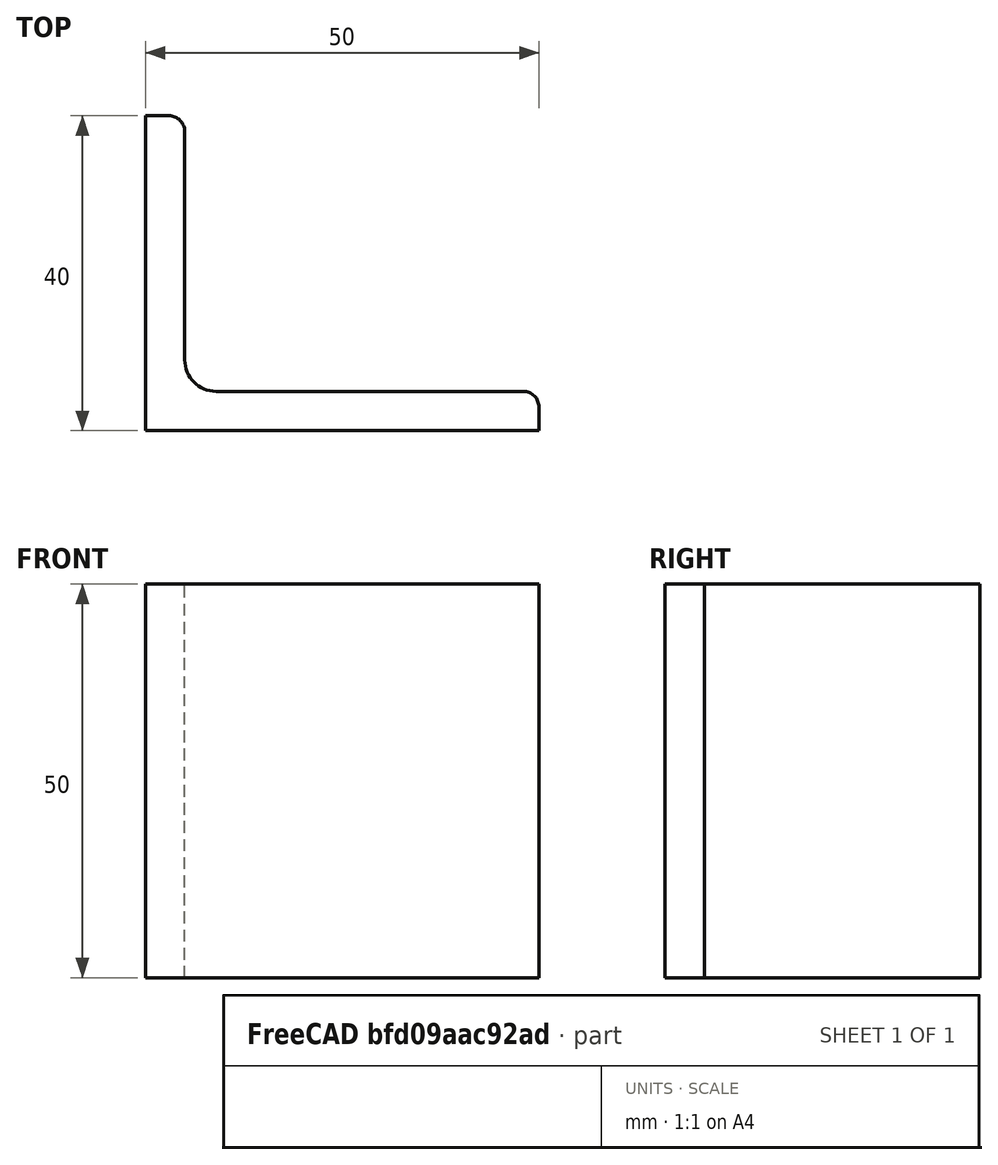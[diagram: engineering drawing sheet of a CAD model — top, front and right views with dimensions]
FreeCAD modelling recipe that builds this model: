
FCSTD DOCUMENT  (FreeCAD 0.15R4671 (Git))
Label: Angle Bar 50x40x5 EN10056 S235JR
License: All rights reserved
LicenseURL: http://en.wikipedia.org/wiki/All_rights_reserved
objects: Sketcher::SketchObject×1, Part::Extrusion×1
note: 2 computed .brp shape members not serialized (recipe doc carries the construction recipe); baked Part::Feature solids carry a one-line shape summary decoded from their .brp

FEATURE [Sketcher::SketchObject] Sketch
  sketch-geometry (9):
    g0: LineSegment StartX=0 StartY=0 StartZ=0 EndX=50 EndY=0 EndZ=0
    g1: LineSegment StartX=50 StartY=0 StartZ=0 EndX=50 EndY=3 EndZ=0
    g2: LineSegment StartX=48 StartY=5 StartZ=0 EndX=9 EndY=5 EndZ=0
    g3: LineSegment StartX=0 StartY=0 StartZ=0 EndX=0 EndY=40 EndZ=0
    g4: LineSegment StartX=0 StartY=40 StartZ=0 EndX=3 EndY=40 EndZ=0
    g5: LineSegment StartX=5 StartY=38 StartZ=0 EndX=5 EndY=9 EndZ=0
    g6: ArcOfCircle CenterX=9 CenterY=9 CenterZ=0 NormalX=0 NormalY=0 NormalZ=1 Radius=4 StartAngle=3.14159 EndAngle=4.71239
    g7: ArcOfCircle CenterX=3 CenterY=38 CenterZ=0 NormalX=0 NormalY=0 NormalZ=1 Radius=2 StartAngle=0 EndAngle=1.5708
    g8: ArcOfCircle CenterX=48 CenterY=3 CenterZ=0 NormalX=0 NormalY=0 NormalZ=1 Radius=2 StartAngle=0 EndAngle=1.5708
  constraints (23):
    c: Coincident(g0,g-1)
    c: Horizontal(g0)
    c: Coincident(g1,g0)
    c: Vertical(g1)
    c: Horizontal(g2)
    c: Coincident(g3,g-1)
    c: Vertical(g3)
    c: Coincident(g4,g3)
    c: Horizontal(g4)
    c: Vertical(g5)
    c: Tangent(g5,g6) = -1.5708
    c: Tangent(g2,g6) = 1.5708
    c: Tangent(g4,g7) = 1.5708
    c: Tangent(g5,g7) = 1.5708
    c: Tangent(g2,g8) = -1.5708
    c: Tangent(g1,g8) = -1.5708
    c: DistanceX(g0) = 50
    c: DistanceY(g3) = 40
    c: DistanceY(g0,g2) = 5
    c: DistanceX(g3,g5) = 5
    c: Radius(g6) = 4
    c: Radius(g8) = 2
    c: Radius(g7) = 2
FEATURE [Part::Extrusion] Extrude  label="Angle Bar 50x40x5 EN10056 S235JR"
  Base = -> Sketch
  Dir = (0,0,50)
  Solid = true
